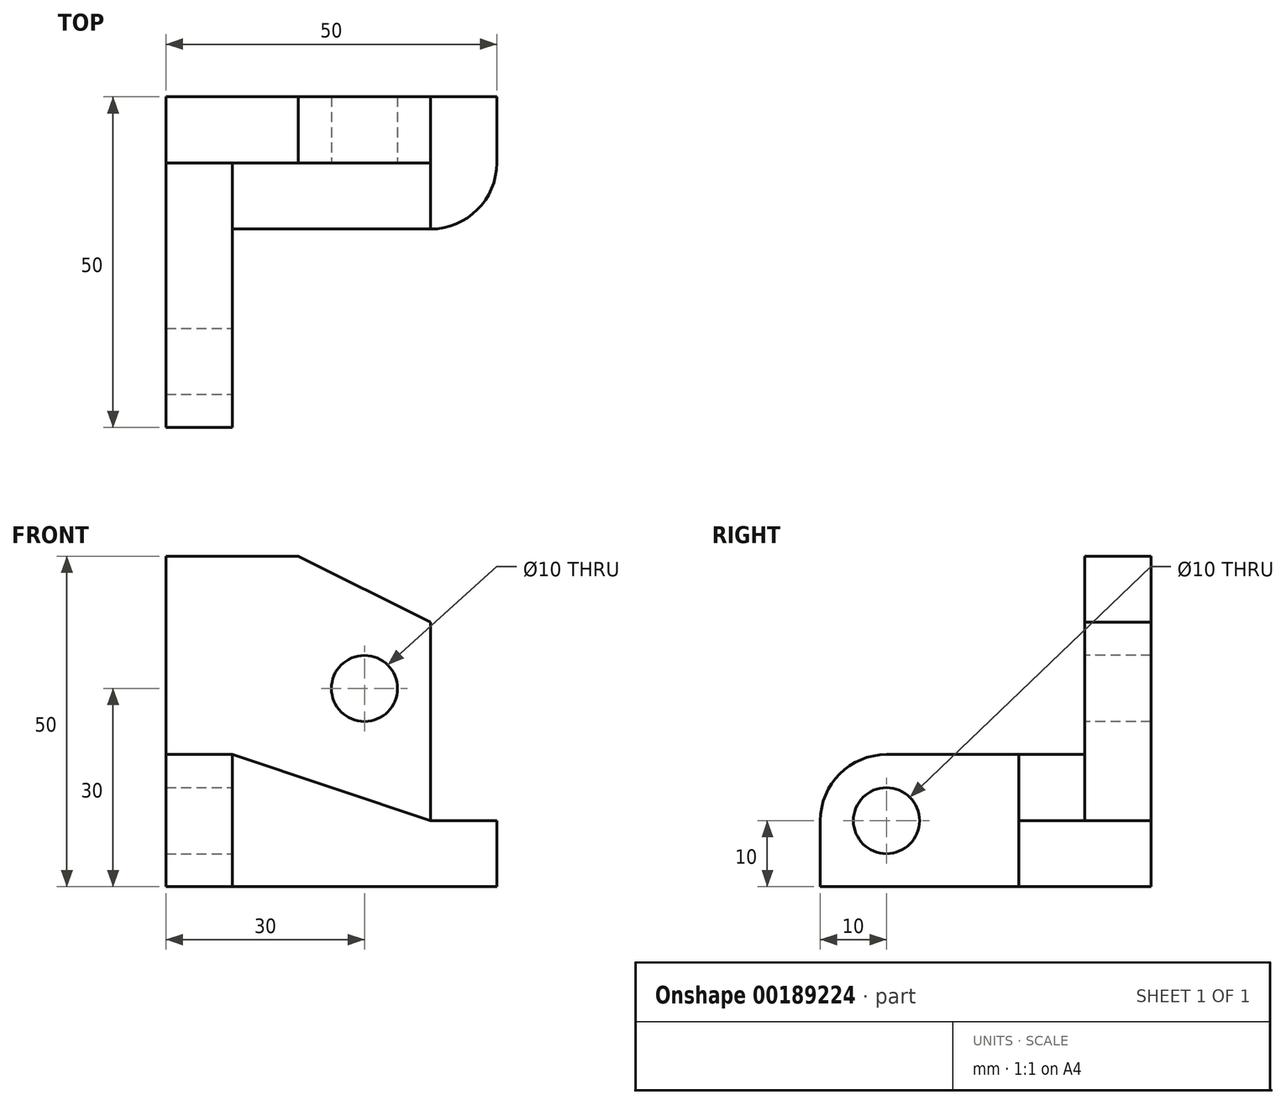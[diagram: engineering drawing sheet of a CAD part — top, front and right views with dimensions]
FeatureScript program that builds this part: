
annotation { "Feature Type Name" : "Feature", "Feature Type Description" : "" }
export const myFeature = defineFeature(function(context is Context, id is Id, definition is map)
    precondition{}
    {
        {
            var Q0;
            Q0=qCreatedBy(makeId("Front.planeOp"),FACE);
            var sketch = newSketch(context, id + "F0", { "sketchPlane" : qUnion([Q0])});
            skLineSegment(sketch, "E0", {"start": v(0, 0) * mm, "end": v(0, 50) * mm});
            skLineSegment(sketch, "E1", {"start": v(0, 50) * mm, "end": v(20, 50) * mm});
            skLineSegment(sketch, "E2", {"start": v(20, 50) * mm, "end": v(40, 40) * mm});
            skLineSegment(sketch, "E3", {"start": v(40, 40) * mm, "end": v(40, 10) * mm});
            skLineSegment(sketch, "E4", {"start": v(40, 10) * mm, "end": v(50, 10) * mm});
            skLineSegment(sketch, "E5", {"start": v(50, 10) * mm, "end": v(50, 0) * mm});
            skLineSegment(sketch, "E6", {"start": v(50, 0) * mm, "end": v(0, 0) * mm});
            skSolve(sketch);
        }
        {
            var Q0;
            Q0=makeQuery(id+"F0.imprint","IMPRINT",FACE,{"disambiguationData":[TD([[makeQuery(id+"F0.imprint","IMPRINT",EDGE,{"derivedFrom":sQuery(id+"F0.wireOp",EDGE,"E0")}),-1.0]])]});
            extrude(context, id + "F1", {"entities" : qUnion([Q0]), "depth" : 10 * mm});
        }
        {
            var Q0;
            Q0=makeQuery(id+"F1.opExtrude","CAP_FACE",FACE,{"disambiguationData":[OSD([sQuery(id+"F0.wireOp",EDGE,"E0"),sQuery(id+"F0.wireOp",EDGE,"E1"),sQuery(id+"F0.wireOp",EDGE,"E2"),sQuery(id+"F0.wireOp",EDGE,"E3"),sQuery(id+"F0.wireOp",EDGE,"E4"),sQuery(id+"F0.wireOp",EDGE,"E5"),sQuery(id+"F0.wireOp",EDGE,"E6")])],"isStart":false});
            var sketch = newSketch(context, id + "F2", { "sketchPlane" : qUnion([Q0])});
            skLineSegment(sketch, "E7.0", {"start": v(0, 0) * mm, "end": v(0, 20) * mm});
            skLineSegment(sketch, "E8.0", {"start": v(50, 0) * mm, "end": v(0, 0) * mm});
            skLineSegment(sketch, "E9.0", {"start": v(50, 10) * mm, "end": v(50, 0) * mm});
            skLineSegment(sketch, "E10.0", {"start": v(40, 10) * mm, "end": v(50, 10) * mm});
            skLineSegment(sketch, "E11", {"start": v(40, 10) * mm, "end": v(10, 20) * mm});
            skLineSegment(sketch, "E12", {"start": v(10, 20) * mm, "end": v(0, 20) * mm});
            skPoint(sketch, "E13.orphan", {"position": v(0, 50) * mm});
            skSolve(sketch);
        }
        {
            var Q0;
            Q0=makeQuery(id+"F2.imprint","IMPRINT",FACE,{"disambiguationData":[TD([[makeQuery(id+"F2.imprint","IMPRINT",EDGE,{"derivedFrom":sQuery(id+"F2.wireOp",EDGE,"E7.0")}),-1.0]])]});
            extrude(context, id + "F3", {"entities" : qUnion([Q0]), "operationType" : NewBodyOperationType.ADD, "depth" : 10 * mm});
        }
        {
            var Q0;
            Q0=makeQuery(id+"F1.opExtrude","CAP_FACE",FACE,{"disambiguationData":[OSD([sQuery(id+"F0.wireOp",EDGE,"E0"),sQuery(id+"F0.wireOp",EDGE,"E1"),sQuery(id+"F0.wireOp",EDGE,"E2"),sQuery(id+"F0.wireOp",EDGE,"E3"),sQuery(id+"F0.wireOp",EDGE,"E4"),sQuery(id+"F0.wireOp",EDGE,"E5"),sQuery(id+"F0.wireOp",EDGE,"E6")])],"isStart":false});
            var sketch = newSketch(context, id + "F4", { "sketchPlane" : qUnion([Q0])});
            skCircle(sketch, "E14", {"center": v(30, 30) * mm, "radius": 5 * mm});
            skSolve(sketch);
        }
        {
            var Q0;
            Q0=makeQuery(id+"F4.imprint","IMPRINT",FACE,{"disambiguationData":[TD([[makeQuery(id+"F4.imprint","IMPRINT",EDGE,{"derivedFrom":sQuery(id+"F4.wireOp",EDGE,"E14")}),1.0]])]});
            extrude(context, id + "F5", {"entities" : qUnion([Q0]), "operationType" : NewBodyOperationType.REMOVE, "endBound" : BoundingType.UP_TO_NEXT, "oppositeDirection" : true, "depth" : 25 * mm});
        }
        {
            var Q0;
            Q0=makeQuery(id+"F3.opExtrude","CAP_FACE",FACE,{"disambiguationData":[OSD([sQuery(id+"F2.wireOp",EDGE,"E7.0"),sQuery(id+"F2.wireOp",EDGE,"E8.0"),sQuery(id+"F2.wireOp",EDGE,"E9.0"),sQuery(id+"F2.wireOp",EDGE,"E10.0"),sQuery(id+"F2.wireOp",EDGE,"E11"),sQuery(id+"F2.wireOp",EDGE,"E12")])],"isStart":false});
            var sketch = newSketch(context, id + "F6", { "sketchPlane" : qUnion([Q0])});
            skLineSegment(sketch, "E15.0", {"start": v(0, 0) * mm, "end": v(0, 20) * mm});
            skPoint(sketch, "E16.0", {"position": v(5, 20) * mm});
            skLineSegment(sketch, "E17.0", {"start": v(10, 20) * mm, "end": v(0, 20) * mm});
            skLineSegment(sketch, "E18.0", {"start": v(10, 0) * mm, "end": v(0, 0) * mm});
            skLineSegment(sketch, "E19", {"start": v(10, 20) * mm, "end": v(10, 0) * mm});
            skSolve(sketch);
        }
        {
            var Q0;
            Q0=makeQuery(id+"F6.imprint","IMPRINT",FACE,{"disambiguationData":[TD([[makeQuery(id+"F6.imprint","IMPRINT",EDGE,{"derivedFrom":sQuery(id+"F6.wireOp",EDGE,"E15.0")}),-1.0]])]});
            extrude(context, id + "F7", {"entities" : qUnion([Q0]), "operationType" : NewBodyOperationType.ADD, "depth" : 30 * mm});
        }
        {
            var Q0;
            Q0=makeQuery(id+"F3.opExtrude","CAP_EDGE",EDGE,{"disambiguationData":[OSD([sQuery(id+"F2.wireOp",EDGE,"E9.0")])],"isStart":false});
            var Q1;
            Q1=makeQuery(id+"F7.opExtrude","CAP_EDGE",EDGE,{"disambiguationData":[OSD([sQuery(id+"F6.wireOp",EDGE,"E17.0")])],"isStart":false});
            fillet(context, id + "F8", {"entities" : qUnion([Q0, Q1]), "radius" : 10 * mm, "tangentPropagation" : true, "allowEdgeOverflow" : false});
        }
        {
            var Q0;
            Q0=makeQuery(id+"F7.opExtrude","SWEPT_FACE",FACE,{"disambiguationData":[OSD([sQuery(id+"F6.wireOp",EDGE,"E19")])]});
            var sketch = newSketch(context, id + "F9", { "sketchPlane" : qUnion([Q0])});
            skCircle(sketch, "E20", {"center": v(-40, 10) * mm, "radius": 5 * mm});
            skSolve(sketch);
        }
        {
            var Q0;
            Q0=makeQuery(id+"F9.imprint","IMPRINT",FACE,{"disambiguationData":[TD([[makeQuery(id+"F9.imprint","IMPRINT",EDGE,{"derivedFrom":sQuery(id+"F9.wireOp",EDGE,"E20")}),1.0]])]});
            extrude(context, id + "F10", {"entities" : qUnion([Q0]), "operationType" : NewBodyOperationType.REMOVE, "endBound" : BoundingType.UP_TO_NEXT, "oppositeDirection" : true, "depth" : 25 * mm});
        }
    });
